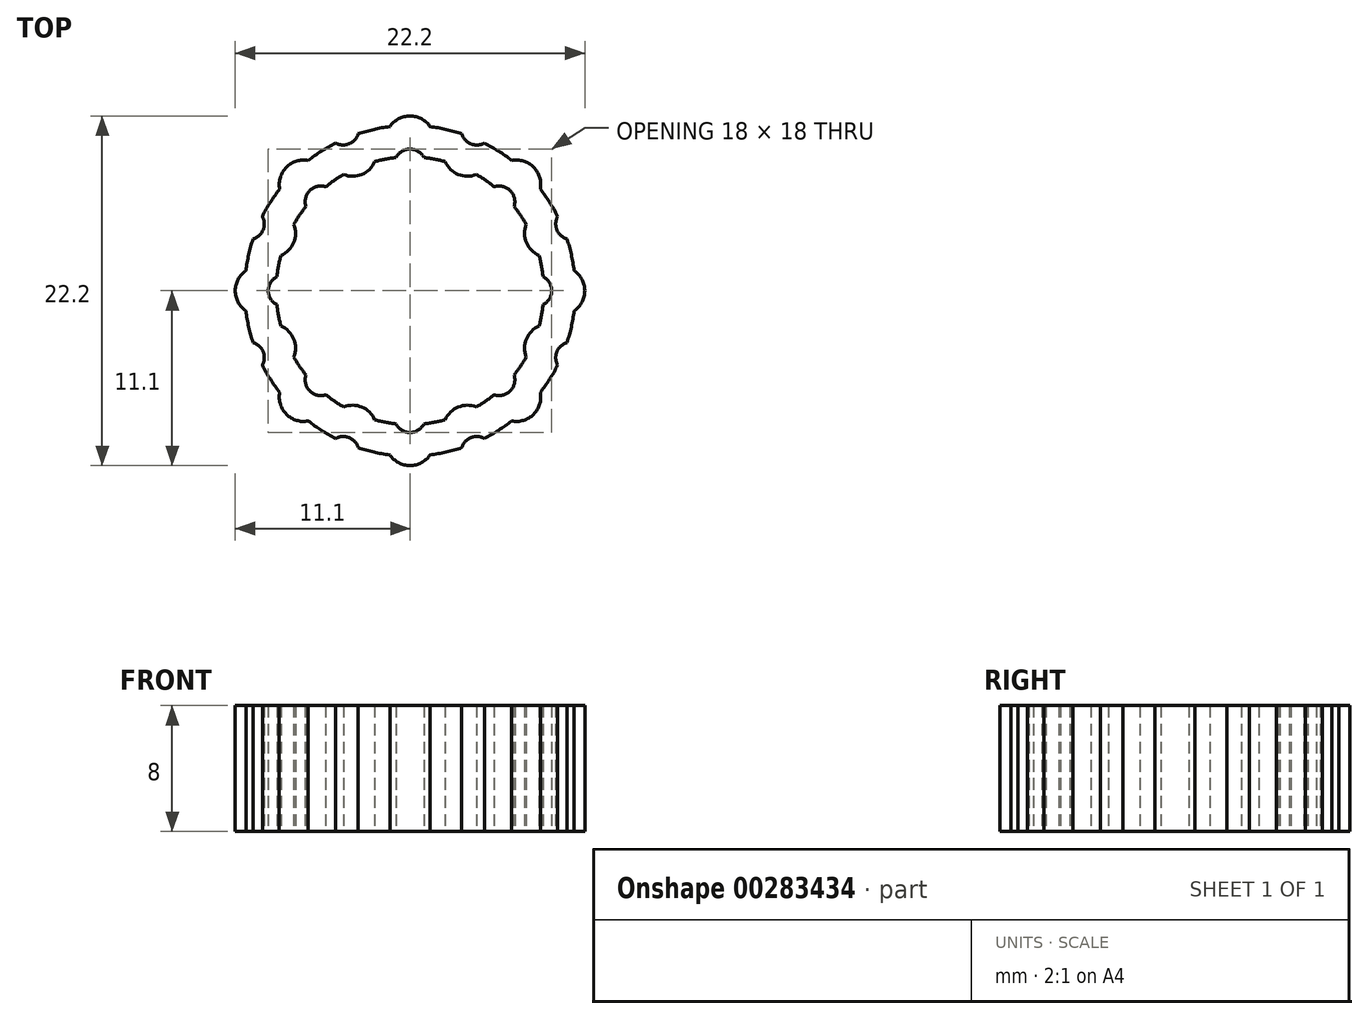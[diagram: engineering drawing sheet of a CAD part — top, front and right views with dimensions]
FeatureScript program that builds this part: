
annotation { "Feature Type Name" : "Feature", "Feature Type Description" : "" }
export const myFeature = defineFeature(function(context is Context, id is Id, definition is map)
    precondition{}
    {
        {
            var Q0;
            Q0=qCreatedBy(makeId("Top.planeOp"),FACE);
            var sketch = newSketch(context, id + "F0", { "sketchPlane" : qUnion([Q0])});
            skCircle(sketch, "E0", {"center": v(0, 0) * mm, "radius": 11.1 * mm});
            skCircle(sketch, "E1", {"center": v(0, 0) * mm, "radius": 8 * mm});
            skCircle(sketch, "E2", {"center": v(0, 9.55) * mm, "radius": 1.55 * mm});
            skCircle(sketch, "E3", {"center": v(0, 0) * mm, "radius": 10.5 * mm});
            skCircle(sketch, "E4.1.0", {"center": v(-3.65, 8.82) * mm, "radius": 1.55 * mm});
            skCircle(sketch, "E4.2.0", {"center": v(-6.75, 6.75) * mm, "radius": 1.55 * mm});
            skCircle(sketch, "E4.3.0", {"center": v(-8.82, 3.65) * mm, "radius": 1.55 * mm});
            skCircle(sketch, "E4.4.0", {"center": v(-9.55, 0) * mm, "radius": 1.55 * mm});
            skCircle(sketch, "E4.5.0", {"center": v(-8.82, -3.65) * mm, "radius": 1.55 * mm});
            skCircle(sketch, "E4.6.0", {"center": v(-6.75, -6.75) * mm, "radius": 1.55 * mm});
            skCircle(sketch, "E4.7.0", {"center": v(-3.65, -8.82) * mm, "radius": 1.55 * mm});
            skCircle(sketch, "E5.1.8.0", {"center": v(0, -9.55) * mm, "radius": 1.55 * mm});
            skCircle(sketch, "E5.1.9.0", {"center": v(3.65, -8.82) * mm, "radius": 1.55 * mm});
            skCircle(sketch, "E5.1.10.0", {"center": v(6.75, -6.75) * mm, "radius": 1.55 * mm});
            skCircle(sketch, "E5.1.11.0", {"center": v(8.82, -3.65) * mm, "radius": 1.55 * mm});
            skCircle(sketch, "E6", {"center": v(0, 0) * mm, "radius": 8.5 * mm});
            skCircle(sketch, "E7.1.12.0", {"center": v(9.55, 0) * mm, "radius": 1.55 * mm});
            skCircle(sketch, "E8.1.13.0", {"center": v(8.82, 3.65) * mm, "radius": 1.55 * mm});
            skCircle(sketch, "E9.1.14.0", {"center": v(6.75, 6.75) * mm, "radius": 1.55 * mm});
            skCircle(sketch, "E9.1.15.0", {"center": v(3.65, 8.82) * mm, "radius": 1.55 * mm});
            skCircle(sketch, "E10", {"center": v(0, 8) * mm, "radius": 1 * mm});
            skCircle(sketch, "E11.1.0", {"center": v(-5.66, 5.66) * mm, "radius": 1 * mm});
            skCircle(sketch, "E11.2.0", {"center": v(-8, 0) * mm, "radius": 1 * mm});
            skCircle(sketch, "E11.3.0", {"center": v(-5.66, -5.66) * mm, "radius": 1 * mm});
            skCircle(sketch, "E11.4.0", {"center": v(0, -8) * mm, "radius": 1 * mm});
            skCircle(sketch, "E11.5.0", {"center": v(5.66, -5.66) * mm, "radius": 1 * mm});
            skCircle(sketch, "E11.6.0", {"center": v(8, 0) * mm, "radius": 1 * mm});
            skCircle(sketch, "E11.7.0", {"center": v(5.66, 5.66) * mm, "radius": 1 * mm});
            skCircle(sketch, "E12", {"center": v(-4.25, 10.26) * mm, "radius": 1 * mm});
            skCircle(sketch, "E13.1.0", {"center": v(-10.26, 4.25) * mm, "radius": 1 * mm});
            skCircle(sketch, "E13.2.0", {"center": v(-10.26, -4.25) * mm, "radius": 1 * mm});
            skCircle(sketch, "E13.3.0", {"center": v(-4.25, -10.26) * mm, "radius": 1 * mm});
            skCircle(sketch, "E13.4.0", {"center": v(4.25, -10.26) * mm, "radius": 1 * mm});
            skCircle(sketch, "E13.5.0", {"center": v(10.26, -4.25) * mm, "radius": 1 * mm});
            skCircle(sketch, "E13.6.0", {"center": v(10.26, 4.25) * mm, "radius": 1 * mm});
            skCircle(sketch, "E13.7.0", {"center": v(4.25, 10.26) * mm, "radius": 1 * mm});
            skSolve(sketch);
        }
        {
            var Q0;
            {var subQ5=sQuery(id+"F0.wireOp",EDGE,"E3");var subQ6=sQuery(id+"F0.wireOp",EDGE,"E2");var subQ7=makeQuery(id+"F0.imprint","INTERSECT",VERTEX,{"disambiguationData":[OD(1.0)],"derivedFrom":[subQ6,subQ5]});Q0=makeQuery(id+"F0.imprint","IMPRINT",FACE,{"disambiguationData":[TD([[makeQuery(id+"F0.imprint","IMPRINT",EDGE,{"disambiguationData":[TD([[subQ7,-1.0]])],"derivedFrom":subQ6}),-1.0]])]});}
            var Q1;
            {var subQ0=sQuery(id+"F0.wireOp",EDGE,"E3");var subQ1=sQuery(id+"F0.wireOp",EDGE,"E2");var subQ2=makeQuery(id+"F0.imprint","INTERSECT",VERTEX,{"disambiguationData":[OD(1.0)],"derivedFrom":[subQ1,subQ0]});Q1=makeQuery(id+"F0.imprint","IMPRINT",FACE,{"disambiguationData":[TD([[makeQuery(id+"F0.imprint","IMPRINT",EDGE,{"disambiguationData":[TD([[subQ2,-1.0]])],"derivedFrom":subQ1}),1.0]])]});}
            var Q2;
            {var subQ0=sQuery(id+"F0.wireOp",EDGE,"E2");var subQ1=makeQuery(id+"F0.imprint","INTERSECT",VERTEX,{"derivedFrom":[sQuery(id+"F0.wireOp",EDGE,"E0"),subQ0]});Q2=makeQuery(id+"F0.imprint","IMPRINT",FACE,{"disambiguationData":[TD([[makeQuery(id+"F0.imprint","IMPRINT",EDGE,{"disambiguationData":[TD([[subQ1,1.0]])],"derivedFrom":subQ0}),1.0]])]});}
            var Q3;
            {var subQ7=sQuery(id+"F0.wireOp",EDGE,"E3");var subQ8=sQuery(id+"F0.wireOp",EDGE,"E2");var subQ9=makeQuery(id+"F0.imprint","INTERSECT",VERTEX,{"disambiguationData":[OD(0.0)],"derivedFrom":[subQ8,subQ7]});Q3=makeQuery(id+"F0.imprint","IMPRINT",FACE,{"disambiguationData":[TD([[makeQuery(id+"F0.imprint","IMPRINT",EDGE,{"disambiguationData":[TD([[subQ9,1.0]])],"derivedFrom":subQ8}),-1.0]])]});}
            var Q4;
            {var subQ0=sQuery(id+"F0.wireOp",EDGE,"E9.1.15.0");var subQ1=sQuery(id+"F0.wireOp",EDGE,"E6");var subQ2=makeQuery(id+"F0.imprint","INTERSECT",VERTEX,{"disambiguationData":[OD(0.0)],"derivedFrom":[subQ1,subQ0]});Q4=makeQuery(id+"F0.imprint","IMPRINT",FACE,{"disambiguationData":[TD([[makeQuery(id+"F0.imprint","IMPRINT",EDGE,{"disambiguationData":[TD([[subQ2,-1.0]])],"derivedFrom":subQ1}),-1.0]])]});}
            var Q5;
            {var subQ0=sQuery(id+"F0.wireOp",EDGE,"E9.1.15.0");var subQ1=sQuery(id+"F0.wireOp",EDGE,"E6");var subQ2=makeQuery(id+"F0.imprint","INTERSECT",VERTEX,{"disambiguationData":[OD(0.0)],"derivedFrom":[subQ1,subQ0]});Q5=makeQuery(id+"F0.imprint","IMPRINT",FACE,{"disambiguationData":[TD([[makeQuery(id+"F0.imprint","IMPRINT",EDGE,{"disambiguationData":[TD([[subQ2,-1.0]])],"derivedFrom":subQ1}),1.0]])]});}
            var Q6;
            {var subQ5=sQuery(id+"F0.wireOp",EDGE,"E9.1.14.0");var subQ6=sQuery(id+"F0.wireOp",EDGE,"E3");var subQ7=makeQuery(id+"F0.imprint","INTERSECT",VERTEX,{"disambiguationData":[OD(1.0)],"derivedFrom":[subQ6,subQ5]});Q6=makeQuery(id+"F0.imprint","IMPRINT",FACE,{"disambiguationData":[TD([[makeQuery(id+"F0.imprint","IMPRINT",EDGE,{"disambiguationData":[TD([[subQ7,-1.0]])],"derivedFrom":subQ6}),1.0]])]});}
            var Q7;
            {var subQ0=sQuery(id+"F0.wireOp",EDGE,"E9.1.14.0");var subQ1=sQuery(id+"F0.wireOp",EDGE,"E3");var subQ2=makeQuery(id+"F0.imprint","INTERSECT",VERTEX,{"disambiguationData":[OD(0.0)],"derivedFrom":[subQ1,subQ0]});Q7=makeQuery(id+"F0.imprint","IMPRINT",FACE,{"disambiguationData":[TD([[makeQuery(id+"F0.imprint","IMPRINT",EDGE,{"disambiguationData":[TD([[subQ2,-1.0]])],"derivedFrom":subQ1}),1.0]])]});}
            var Q8;
            {var subQ0=sQuery(id+"F0.wireOp",EDGE,"E9.1.14.0");var subQ1=sQuery(id+"F0.wireOp",EDGE,"E3");var subQ2=makeQuery(id+"F0.imprint","INTERSECT",VERTEX,{"disambiguationData":[OD(0.0)],"derivedFrom":[subQ1,subQ0]});Q8=makeQuery(id+"F0.imprint","IMPRINT",FACE,{"disambiguationData":[TD([[makeQuery(id+"F0.imprint","IMPRINT",EDGE,{"disambiguationData":[TD([[subQ2,-1.0]])],"derivedFrom":subQ1}),-1.0]])]});}
            var Q9;
            {var subQ1=sQuery(id+"F0.wireOp",EDGE,"E3");var subQ8=sQuery(id+"F0.wireOp",EDGE,"E13.6.0");var subQ11=makeQuery(id+"F0.imprint","INTERSECT",VERTEX,{"disambiguationData":[OD(1.0)],"derivedFrom":[subQ1,subQ8]});Q9=makeQuery(id+"F0.imprint","IMPRINT",FACE,{"disambiguationData":[TD([[makeQuery(id+"F0.imprint","IMPRINT",EDGE,{"disambiguationData":[TD([[subQ11,-1.0]])],"derivedFrom":subQ1}),1.0]])]});}
            var Q10;
            {var subQ0=sQuery(id+"F0.wireOp",EDGE,"E8.1.13.0");var subQ1=sQuery(id+"F0.wireOp",EDGE,"E6");var subQ2=makeQuery(id+"F0.imprint","INTERSECT",VERTEX,{"disambiguationData":[OD(0.0)],"derivedFrom":[subQ1,subQ0]});Q10=makeQuery(id+"F0.imprint","IMPRINT",FACE,{"disambiguationData":[TD([[makeQuery(id+"F0.imprint","IMPRINT",EDGE,{"disambiguationData":[TD([[subQ2,-1.0]])],"derivedFrom":subQ1}),-1.0]])]});}
            var Q11;
            {var subQ0=sQuery(id+"F0.wireOp",EDGE,"E8.1.13.0");var subQ1=sQuery(id+"F0.wireOp",EDGE,"E6");var subQ2=makeQuery(id+"F0.imprint","INTERSECT",VERTEX,{"disambiguationData":[OD(0.0)],"derivedFrom":[subQ1,subQ0]});Q11=makeQuery(id+"F0.imprint","IMPRINT",FACE,{"disambiguationData":[TD([[makeQuery(id+"F0.imprint","IMPRINT",EDGE,{"disambiguationData":[TD([[subQ2,-1.0]])],"derivedFrom":subQ1}),1.0]])]});}
            var Q12;
            {var subQ0=sQuery(id+"F0.wireOp",EDGE,"E5.1.11.0");var subQ1=makeQuery(id+"F0.imprint","INTERSECT",VERTEX,{"derivedFrom":[sQuery(id+"F0.wireOp",EDGE,"E1"),subQ0]});Q12=makeQuery(id+"F0.imprint","IMPRINT",FACE,{"disambiguationData":[TD([[makeQuery(id+"F0.imprint","IMPRINT",EDGE,{"disambiguationData":[TD([[subQ1,1.0]])],"derivedFrom":subQ0}),1.0]])]});}
            var Q13;
            {var subQ0=sQuery(id+"F0.wireOp",EDGE,"E5.1.9.0");var subQ1=makeQuery(id+"F0.imprint","INTERSECT",VERTEX,{"derivedFrom":[sQuery(id+"F0.wireOp",EDGE,"E1"),subQ0]});Q13=makeQuery(id+"F0.imprint","IMPRINT",FACE,{"disambiguationData":[TD([[makeQuery(id+"F0.imprint","IMPRINT",EDGE,{"disambiguationData":[TD([[subQ1,1.0]])],"derivedFrom":subQ0}),1.0]])]});}
            var Q14;
            {var subQ0=sQuery(id+"F0.wireOp",EDGE,"E4.7.0");var subQ1=makeQuery(id+"F0.imprint","INTERSECT",VERTEX,{"derivedFrom":[sQuery(id+"F0.wireOp",EDGE,"E1"),subQ0]});Q14=makeQuery(id+"F0.imprint","IMPRINT",FACE,{"disambiguationData":[TD([[makeQuery(id+"F0.imprint","IMPRINT",EDGE,{"disambiguationData":[TD([[subQ1,1.0]])],"derivedFrom":subQ0}),1.0]])]});}
            var Q15;
            {var subQ0=sQuery(id+"F0.wireOp",EDGE,"E4.5.0");var subQ1=makeQuery(id+"F0.imprint","INTERSECT",VERTEX,{"derivedFrom":[sQuery(id+"F0.wireOp",EDGE,"E1"),subQ0]});Q15=makeQuery(id+"F0.imprint","IMPRINT",FACE,{"disambiguationData":[TD([[makeQuery(id+"F0.imprint","IMPRINT",EDGE,{"disambiguationData":[TD([[subQ1,1.0]])],"derivedFrom":subQ0}),1.0]])]});}
            var Q16;
            {var subQ0=sQuery(id+"F0.wireOp",EDGE,"E4.3.0");var subQ1=makeQuery(id+"F0.imprint","INTERSECT",VERTEX,{"derivedFrom":[sQuery(id+"F0.wireOp",EDGE,"E1"),subQ0]});Q16=makeQuery(id+"F0.imprint","IMPRINT",FACE,{"disambiguationData":[TD([[makeQuery(id+"F0.imprint","IMPRINT",EDGE,{"disambiguationData":[TD([[subQ1,1.0]])],"derivedFrom":subQ0}),1.0]])]});}
            var Q17;
            {var subQ0=sQuery(id+"F0.wireOp",EDGE,"E4.1.0");var subQ1=makeQuery(id+"F0.imprint","INTERSECT",VERTEX,{"derivedFrom":[sQuery(id+"F0.wireOp",EDGE,"E1"),subQ0]});Q17=makeQuery(id+"F0.imprint","IMPRINT",FACE,{"disambiguationData":[TD([[makeQuery(id+"F0.imprint","IMPRINT",EDGE,{"disambiguationData":[TD([[subQ1,1.0]])],"derivedFrom":subQ0}),1.0]])]});}
            var Q18;
            {var subQ1=sQuery(id+"F0.wireOp",EDGE,"E3");var subQ5=sQuery(id+"F0.wireOp",EDGE,"E12");var subQ11=makeQuery(id+"F0.imprint","INTERSECT",VERTEX,{"disambiguationData":[OD(1.0)],"derivedFrom":[subQ1,subQ5]});Q18=makeQuery(id+"F0.imprint","IMPRINT",FACE,{"disambiguationData":[TD([[makeQuery(id+"F0.imprint","IMPRINT",EDGE,{"disambiguationData":[TD([[subQ11,-1.0]])],"derivedFrom":subQ1}),1.0]])]});}
            var Q19;
            {var subQ0=sQuery(id+"F0.wireOp",EDGE,"E4.2.0");var subQ1=sQuery(id+"F0.wireOp",EDGE,"E3");var subQ2=makeQuery(id+"F0.imprint","INTERSECT",VERTEX,{"disambiguationData":[OD(0.0)],"derivedFrom":[subQ1,subQ0]});Q19=makeQuery(id+"F0.imprint","IMPRINT",FACE,{"disambiguationData":[TD([[makeQuery(id+"F0.imprint","IMPRINT",EDGE,{"disambiguationData":[TD([[subQ2,-1.0]])],"derivedFrom":subQ1}),1.0]])]});}
            var Q20;
            {var subQ7=sQuery(id+"F0.wireOp",EDGE,"E4.2.0");var subQ8=sQuery(id+"F0.wireOp",EDGE,"E3");var subQ9=makeQuery(id+"F0.imprint","INTERSECT",VERTEX,{"disambiguationData":[OD(1.0)],"derivedFrom":[subQ8,subQ7]});Q20=makeQuery(id+"F0.imprint","IMPRINT",FACE,{"disambiguationData":[TD([[makeQuery(id+"F0.imprint","IMPRINT",EDGE,{"disambiguationData":[TD([[subQ9,-1.0]])],"derivedFrom":subQ8}),1.0]])]});}
            var Q21;
            {var subQ1=sQuery(id+"F0.wireOp",EDGE,"E3");var subQ5=sQuery(id+"F0.wireOp",EDGE,"E13.1.0");var subQ11=makeQuery(id+"F0.imprint","INTERSECT",VERTEX,{"disambiguationData":[OD(1.0)],"derivedFrom":[subQ1,subQ5]});Q21=makeQuery(id+"F0.imprint","IMPRINT",FACE,{"disambiguationData":[TD([[makeQuery(id+"F0.imprint","IMPRINT",EDGE,{"disambiguationData":[TD([[subQ11,-1.0]])],"derivedFrom":subQ1}),1.0]])]});}
            var Q22;
            {var subQ0=sQuery(id+"F0.wireOp",EDGE,"E4.4.0");var subQ1=sQuery(id+"F0.wireOp",EDGE,"E3");var subQ2=makeQuery(id+"F0.imprint","INTERSECT",VERTEX,{"disambiguationData":[OD(0.0)],"derivedFrom":[subQ1,subQ0]});Q22=makeQuery(id+"F0.imprint","IMPRINT",FACE,{"disambiguationData":[TD([[makeQuery(id+"F0.imprint","IMPRINT",EDGE,{"disambiguationData":[TD([[subQ2,-1.0]])],"derivedFrom":subQ1}),1.0]])]});}
            var Q23;
            {var subQ7=sQuery(id+"F0.wireOp",EDGE,"E4.4.0");var subQ9=sQuery(id+"F0.wireOp",EDGE,"E3");var subQ10=makeQuery(id+"F0.imprint","INTERSECT",VERTEX,{"disambiguationData":[OD(1.0)],"derivedFrom":[subQ9,subQ7]});Q23=makeQuery(id+"F0.imprint","IMPRINT",FACE,{"disambiguationData":[TD([[makeQuery(id+"F0.imprint","IMPRINT",EDGE,{"disambiguationData":[TD([[subQ10,-1.0]])],"derivedFrom":subQ9}),1.0]])]});}
            var Q24;
            {var subQ1=sQuery(id+"F0.wireOp",EDGE,"E3");var subQ5=sQuery(id+"F0.wireOp",EDGE,"E13.2.0");var subQ11=makeQuery(id+"F0.imprint","INTERSECT",VERTEX,{"disambiguationData":[OD(1.0)],"derivedFrom":[subQ1,subQ5]});Q24=makeQuery(id+"F0.imprint","IMPRINT",FACE,{"disambiguationData":[TD([[makeQuery(id+"F0.imprint","IMPRINT",EDGE,{"disambiguationData":[TD([[subQ11,-1.0]])],"derivedFrom":subQ1}),1.0]])]});}
            var Q25;
            {var subQ0=sQuery(id+"F0.wireOp",EDGE,"E4.6.0");var subQ1=sQuery(id+"F0.wireOp",EDGE,"E3");var subQ2=makeQuery(id+"F0.imprint","INTERSECT",VERTEX,{"disambiguationData":[OD(0.0)],"derivedFrom":[subQ1,subQ0]});Q25=makeQuery(id+"F0.imprint","IMPRINT",FACE,{"disambiguationData":[TD([[makeQuery(id+"F0.imprint","IMPRINT",EDGE,{"disambiguationData":[TD([[subQ2,-1.0]])],"derivedFrom":subQ1}),1.0]])]});}
            var Q26;
            {var subQ5=sQuery(id+"F0.wireOp",EDGE,"E4.6.0");var subQ6=sQuery(id+"F0.wireOp",EDGE,"E3");var subQ7=makeQuery(id+"F0.imprint","INTERSECT",VERTEX,{"disambiguationData":[OD(1.0)],"derivedFrom":[subQ6,subQ5]});Q26=makeQuery(id+"F0.imprint","IMPRINT",FACE,{"disambiguationData":[TD([[makeQuery(id+"F0.imprint","IMPRINT",EDGE,{"disambiguationData":[TD([[subQ7,-1.0]])],"derivedFrom":subQ6}),1.0]])]});}
            var Q27;
            {var subQ0=sQuery(id+"F0.wireOp",EDGE,"E4.2.0");var subQ1=sQuery(id+"F0.wireOp",EDGE,"E3");var subQ2=makeQuery(id+"F0.imprint","INTERSECT",VERTEX,{"disambiguationData":[OD(0.0)],"derivedFrom":[subQ1,subQ0]});Q27=makeQuery(id+"F0.imprint","IMPRINT",FACE,{"disambiguationData":[TD([[makeQuery(id+"F0.imprint","IMPRINT",EDGE,{"disambiguationData":[TD([[subQ2,-1.0]])],"derivedFrom":subQ1}),-1.0]])]});}
            var Q28;
            {var subQ0=sQuery(id+"F0.wireOp",EDGE,"E4.4.0");var subQ1=sQuery(id+"F0.wireOp",EDGE,"E3");var subQ2=makeQuery(id+"F0.imprint","INTERSECT",VERTEX,{"disambiguationData":[OD(0.0)],"derivedFrom":[subQ1,subQ0]});Q28=makeQuery(id+"F0.imprint","IMPRINT",FACE,{"disambiguationData":[TD([[makeQuery(id+"F0.imprint","IMPRINT",EDGE,{"disambiguationData":[TD([[subQ2,-1.0]])],"derivedFrom":subQ1}),-1.0]])]});}
            var Q29;
            {var subQ0=sQuery(id+"F0.wireOp",EDGE,"E4.6.0");var subQ1=sQuery(id+"F0.wireOp",EDGE,"E3");var subQ2=makeQuery(id+"F0.imprint","INTERSECT",VERTEX,{"disambiguationData":[OD(0.0)],"derivedFrom":[subQ1,subQ0]});Q29=makeQuery(id+"F0.imprint","IMPRINT",FACE,{"disambiguationData":[TD([[makeQuery(id+"F0.imprint","IMPRINT",EDGE,{"disambiguationData":[TD([[subQ2,-1.0]])],"derivedFrom":subQ1}),-1.0]])]});}
            var Q30;
            {var subQ1=sQuery(id+"F0.wireOp",EDGE,"E3");var subQ5=sQuery(id+"F0.wireOp",EDGE,"E13.3.0");var subQ10=makeQuery(id+"F0.imprint","INTERSECT",VERTEX,{"disambiguationData":[OD(1.0)],"derivedFrom":[subQ1,subQ5]});Q30=makeQuery(id+"F0.imprint","IMPRINT",FACE,{"disambiguationData":[TD([[makeQuery(id+"F0.imprint","IMPRINT",EDGE,{"disambiguationData":[TD([[subQ10,-1.0]])],"derivedFrom":subQ1}),1.0]])]});}
            var Q31;
            {var subQ0=sQuery(id+"F0.wireOp",EDGE,"E5.1.8.0");var subQ1=sQuery(id+"F0.wireOp",EDGE,"E3");var subQ2=makeQuery(id+"F0.imprint","INTERSECT",VERTEX,{"disambiguationData":[OD(0.0)],"derivedFrom":[subQ1,subQ0]});Q31=makeQuery(id+"F0.imprint","IMPRINT",FACE,{"disambiguationData":[TD([[makeQuery(id+"F0.imprint","IMPRINT",EDGE,{"disambiguationData":[TD([[subQ2,-1.0]])],"derivedFrom":subQ1}),1.0]])]});}
            var Q32;
            {var subQ0=sQuery(id+"F0.wireOp",EDGE,"E5.1.8.0");var subQ1=sQuery(id+"F0.wireOp",EDGE,"E3");var subQ2=makeQuery(id+"F0.imprint","INTERSECT",VERTEX,{"disambiguationData":[OD(0.0)],"derivedFrom":[subQ1,subQ0]});Q32=makeQuery(id+"F0.imprint","IMPRINT",FACE,{"disambiguationData":[TD([[makeQuery(id+"F0.imprint","IMPRINT",EDGE,{"disambiguationData":[TD([[subQ2,-1.0]])],"derivedFrom":subQ1}),-1.0]])]});}
            var Q33;
            {var subQ7=sQuery(id+"F0.wireOp",EDGE,"E5.1.8.0");var subQ8=sQuery(id+"F0.wireOp",EDGE,"E3");var subQ9=makeQuery(id+"F0.imprint","INTERSECT",VERTEX,{"disambiguationData":[OD(1.0)],"derivedFrom":[subQ8,subQ7]});Q33=makeQuery(id+"F0.imprint","IMPRINT",FACE,{"disambiguationData":[TD([[makeQuery(id+"F0.imprint","IMPRINT",EDGE,{"disambiguationData":[TD([[subQ9,-1.0]])],"derivedFrom":subQ8}),1.0]])]});}
            var Q34;
            {var subQ0=sQuery(id+"F0.wireOp",EDGE,"E5.1.10.0");var subQ1=sQuery(id+"F0.wireOp",EDGE,"E3");var subQ2=makeQuery(id+"F0.imprint","INTERSECT",VERTEX,{"disambiguationData":[OD(0.0)],"derivedFrom":[subQ1,subQ0]});Q34=makeQuery(id+"F0.imprint","IMPRINT",FACE,{"disambiguationData":[TD([[makeQuery(id+"F0.imprint","IMPRINT",EDGE,{"disambiguationData":[TD([[subQ2,-1.0]])],"derivedFrom":subQ1}),1.0]])]});}
            var Q35;
            {var subQ0=sQuery(id+"F0.wireOp",EDGE,"E5.1.10.0");var subQ1=sQuery(id+"F0.wireOp",EDGE,"E3");var subQ2=makeQuery(id+"F0.imprint","INTERSECT",VERTEX,{"disambiguationData":[OD(0.0)],"derivedFrom":[subQ1,subQ0]});Q35=makeQuery(id+"F0.imprint","IMPRINT",FACE,{"disambiguationData":[TD([[makeQuery(id+"F0.imprint","IMPRINT",EDGE,{"disambiguationData":[TD([[subQ2,-1.0]])],"derivedFrom":subQ1}),-1.0]])]});}
            var Q36;
            {var subQ7=sQuery(id+"F0.wireOp",EDGE,"E5.1.10.0");var subQ8=sQuery(id+"F0.wireOp",EDGE,"E3");var subQ9=makeQuery(id+"F0.imprint","INTERSECT",VERTEX,{"disambiguationData":[OD(1.0)],"derivedFrom":[subQ8,subQ7]});Q36=makeQuery(id+"F0.imprint","IMPRINT",FACE,{"disambiguationData":[TD([[makeQuery(id+"F0.imprint","IMPRINT",EDGE,{"disambiguationData":[TD([[subQ9,-1.0]])],"derivedFrom":subQ8}),1.0]])]});}
            var Q37;
            {var subQ0=sQuery(id+"F0.wireOp",EDGE,"E13.5.0");var subQ6=sQuery(id+"F0.wireOp",EDGE,"E3");var subQ11=makeQuery(id+"F0.imprint","INTERSECT",VERTEX,{"disambiguationData":[OD(1.0)],"derivedFrom":[subQ6,subQ0]});Q37=makeQuery(id+"F0.imprint","IMPRINT",FACE,{"disambiguationData":[TD([[makeQuery(id+"F0.imprint","IMPRINT",EDGE,{"disambiguationData":[TD([[subQ11,-1.0]])],"derivedFrom":subQ6}),1.0]])]});}
            var Q38;
            {var subQ0=sQuery(id+"F0.wireOp",EDGE,"E7.1.12.0");var subQ1=sQuery(id+"F0.wireOp",EDGE,"E3");var subQ2=makeQuery(id+"F0.imprint","INTERSECT",VERTEX,{"disambiguationData":[OD(0.0)],"derivedFrom":[subQ1,subQ0]});Q38=makeQuery(id+"F0.imprint","IMPRINT",FACE,{"disambiguationData":[TD([[makeQuery(id+"F0.imprint","IMPRINT",EDGE,{"disambiguationData":[TD([[subQ2,1.0]])],"derivedFrom":subQ1}),1.0]])]});}
            var Q39;
            {var subQ0=sQuery(id+"F0.wireOp",EDGE,"E7.1.12.0");var subQ1=sQuery(id+"F0.wireOp",EDGE,"E3");var subQ2=makeQuery(id+"F0.imprint","INTERSECT",VERTEX,{"disambiguationData":[OD(0.0)],"derivedFrom":[subQ1,subQ0]});Q39=makeQuery(id+"F0.imprint","IMPRINT",FACE,{"disambiguationData":[TD([[makeQuery(id+"F0.imprint","IMPRINT",EDGE,{"disambiguationData":[TD([[subQ2,1.0]])],"derivedFrom":subQ1}),-1.0]])]});}
            var Q40;
            {var subQ3=sQuery(id+"F0.wireOp",EDGE,"E13.6.0");var subQ9=sQuery(id+"F0.wireOp",EDGE,"E3");var subQ11=makeQuery(id+"F0.imprint","INTERSECT",VERTEX,{"disambiguationData":[OD(0.0)],"derivedFrom":[subQ9,subQ3]});Q40=makeQuery(id+"F0.imprint","IMPRINT",FACE,{"disambiguationData":[TD([[makeQuery(id+"F0.imprint","IMPRINT",EDGE,{"disambiguationData":[TD([[subQ11,1.0]])],"derivedFrom":subQ9}),1.0]])]});}
            var Q41;
            {var subQ1=sQuery(id+"F0.wireOp",EDGE,"E3");var subQ5=sQuery(id+"F0.wireOp",EDGE,"E13.4.0");var subQ11=makeQuery(id+"F0.imprint","INTERSECT",VERTEX,{"disambiguationData":[OD(1.0)],"derivedFrom":[subQ1,subQ5]});Q41=makeQuery(id+"F0.imprint","IMPRINT",FACE,{"disambiguationData":[TD([[makeQuery(id+"F0.imprint","IMPRINT",EDGE,{"disambiguationData":[TD([[subQ11,-1.0]])],"derivedFrom":subQ1}),1.0]])]});}
            var Q42;
            {var subQ0=sQuery(id+"F0.wireOp",EDGE,"E4.1.0");var subQ1=sQuery(id+"F0.wireOp",EDGE,"E3");var subQ2=makeQuery(id+"F0.imprint","INTERSECT",VERTEX,{"disambiguationData":[OD(1.0)],"derivedFrom":[subQ1,subQ0]});Q42=makeQuery(id+"F0.imprint","IMPRINT",FACE,{"disambiguationData":[TD([[makeQuery(id+"F0.imprint","IMPRINT",EDGE,{"disambiguationData":[TD([[subQ2,-1.0]])],"derivedFrom":subQ1}),1.0]])]});}
            var Q43;
            {var subQ0=sQuery(id+"F0.wireOp",EDGE,"E4.3.0");var subQ1=sQuery(id+"F0.wireOp",EDGE,"E3");var subQ2=makeQuery(id+"F0.imprint","INTERSECT",VERTEX,{"disambiguationData":[OD(1.0)],"derivedFrom":[subQ1,subQ0]});Q43=makeQuery(id+"F0.imprint","IMPRINT",FACE,{"disambiguationData":[TD([[makeQuery(id+"F0.imprint","IMPRINT",EDGE,{"disambiguationData":[TD([[subQ2,-1.0]])],"derivedFrom":subQ1}),1.0]])]});}
            var Q44;
            {var subQ0=sQuery(id+"F0.wireOp",EDGE,"E4.5.0");var subQ1=sQuery(id+"F0.wireOp",EDGE,"E3");var subQ2=makeQuery(id+"F0.imprint","INTERSECT",VERTEX,{"disambiguationData":[OD(1.0)],"derivedFrom":[subQ1,subQ0]});Q44=makeQuery(id+"F0.imprint","IMPRINT",FACE,{"disambiguationData":[TD([[makeQuery(id+"F0.imprint","IMPRINT",EDGE,{"disambiguationData":[TD([[subQ2,-1.0]])],"derivedFrom":subQ1}),1.0]])]});}
            var Q45;
            {var subQ0=sQuery(id+"F0.wireOp",EDGE,"E4.7.0");var subQ1=sQuery(id+"F0.wireOp",EDGE,"E3");var subQ2=makeQuery(id+"F0.imprint","INTERSECT",VERTEX,{"disambiguationData":[OD(1.0)],"derivedFrom":[subQ1,subQ0]});Q45=makeQuery(id+"F0.imprint","IMPRINT",FACE,{"disambiguationData":[TD([[makeQuery(id+"F0.imprint","IMPRINT",EDGE,{"disambiguationData":[TD([[subQ2,-1.0]])],"derivedFrom":subQ1}),1.0]])]});}
            var Q46;
            {var subQ0=sQuery(id+"F0.wireOp",EDGE,"E5.1.9.0");var subQ1=sQuery(id+"F0.wireOp",EDGE,"E3");var subQ2=makeQuery(id+"F0.imprint","INTERSECT",VERTEX,{"disambiguationData":[OD(1.0)],"derivedFrom":[subQ1,subQ0]});Q46=makeQuery(id+"F0.imprint","IMPRINT",FACE,{"disambiguationData":[TD([[makeQuery(id+"F0.imprint","IMPRINT",EDGE,{"disambiguationData":[TD([[subQ2,-1.0]])],"derivedFrom":subQ1}),1.0]])]});}
            var Q47;
            {var subQ0=sQuery(id+"F0.wireOp",EDGE,"E5.1.11.0");var subQ1=sQuery(id+"F0.wireOp",EDGE,"E3");var subQ2=makeQuery(id+"F0.imprint","INTERSECT",VERTEX,{"disambiguationData":[OD(1.0)],"derivedFrom":[subQ1,subQ0]});Q47=makeQuery(id+"F0.imprint","IMPRINT",FACE,{"disambiguationData":[TD([[makeQuery(id+"F0.imprint","IMPRINT",EDGE,{"disambiguationData":[TD([[subQ2,-1.0]])],"derivedFrom":subQ1}),1.0]])]});}
            var Q48;
            {var subQ0=sQuery(id+"F0.wireOp",EDGE,"E8.1.13.0");var subQ1=sQuery(id+"F0.wireOp",EDGE,"E3");var subQ2=makeQuery(id+"F0.imprint","INTERSECT",VERTEX,{"disambiguationData":[OD(0.0)],"derivedFrom":[subQ1,subQ0]});Q48=makeQuery(id+"F0.imprint","IMPRINT",FACE,{"disambiguationData":[TD([[makeQuery(id+"F0.imprint","IMPRINT",EDGE,{"disambiguationData":[TD([[subQ2,1.0]])],"derivedFrom":subQ1}),1.0]])]});}
            var Q49;
            {var subQ0=sQuery(id+"F0.wireOp",EDGE,"E8.1.13.0");var subQ1=sQuery(id+"F0.wireOp",EDGE,"E3");var subQ2=makeQuery(id+"F0.imprint","INTERSECT",VERTEX,{"disambiguationData":[OD(1.0)],"derivedFrom":[subQ1,subQ0]});Q49=makeQuery(id+"F0.imprint","IMPRINT",FACE,{"disambiguationData":[TD([[makeQuery(id+"F0.imprint","IMPRINT",EDGE,{"disambiguationData":[TD([[subQ2,-1.0]])],"derivedFrom":subQ1}),1.0]])]});}
            extrude(context, id + "F1", {"entities" : qUnion([Q0, Q1, Q2, Q3, Q4, Q5, Q6, Q7, Q8, Q9, Q10, Q11, Q12, Q13, Q14, Q15, Q16, Q17, Q18, Q19, Q20, Q21, Q22, Q23, Q24, Q25, Q26, Q27, Q28, Q29, Q30, Q31, Q32, Q33, Q34, Q35, Q36, Q37, Q38, Q39, Q40, Q41, Q42, Q43, Q44, Q45, Q46, Q47, Q48, Q49]), "depth" : 8 * mm, "offsetDistance" : 25 * mm});
        }
    });
